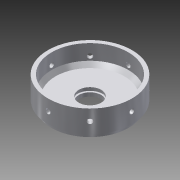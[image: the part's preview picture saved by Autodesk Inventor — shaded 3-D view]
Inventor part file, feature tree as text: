
AUTODESK INVENTOR PART (.ipt)
format: ipt  version: 2015 (Build 190159000, 159)  size: 167,936 bytes
history: native  units: in
note: dims shown in document units (in); Inventor stores cm internally (conversion verified against a paired STEP export)
features: sketch x2, revolve x1, extrude x1, pattern_circular x1
ambient origin geometry x8: Origin, YZ Plane, XZ Plane, XY Plane, X Axis, Y Axis, Z Axis, Center Point
bodies: Body1 (feature_tree)
feature tree (5):
  revolve  "Revolution3"  [1 undecoded]
  extrude  "Extrusion1"  Depth=1.025in
  pattern_circular  "Circular Pattern1"  [2 undecoded]
  sketch  "Sketch1"  dims[d3=0.75in d8=0.5in]
  sketch  "Sketch2"  dims[d9=0.2in d10=0.1182in d11=0.139in d12=0.161in d26=0.234in d28=0.05in d29=0.275in d30=1.5in d31=1.8285in d32=0.05in d35=1.5625in d37=135.0deg d40=2.8125in d41=0.8in d42=1.025in d43=90.0deg d45=0.3125in d46=8.1875in d47=0.0in d48=3.1496in d49=360.0deg]
note: 3 required parameter values undecoded (feature->parameter linkage not recoverable at this tier; creation-order binding heuristic only, values carry confidence <= 0.55)